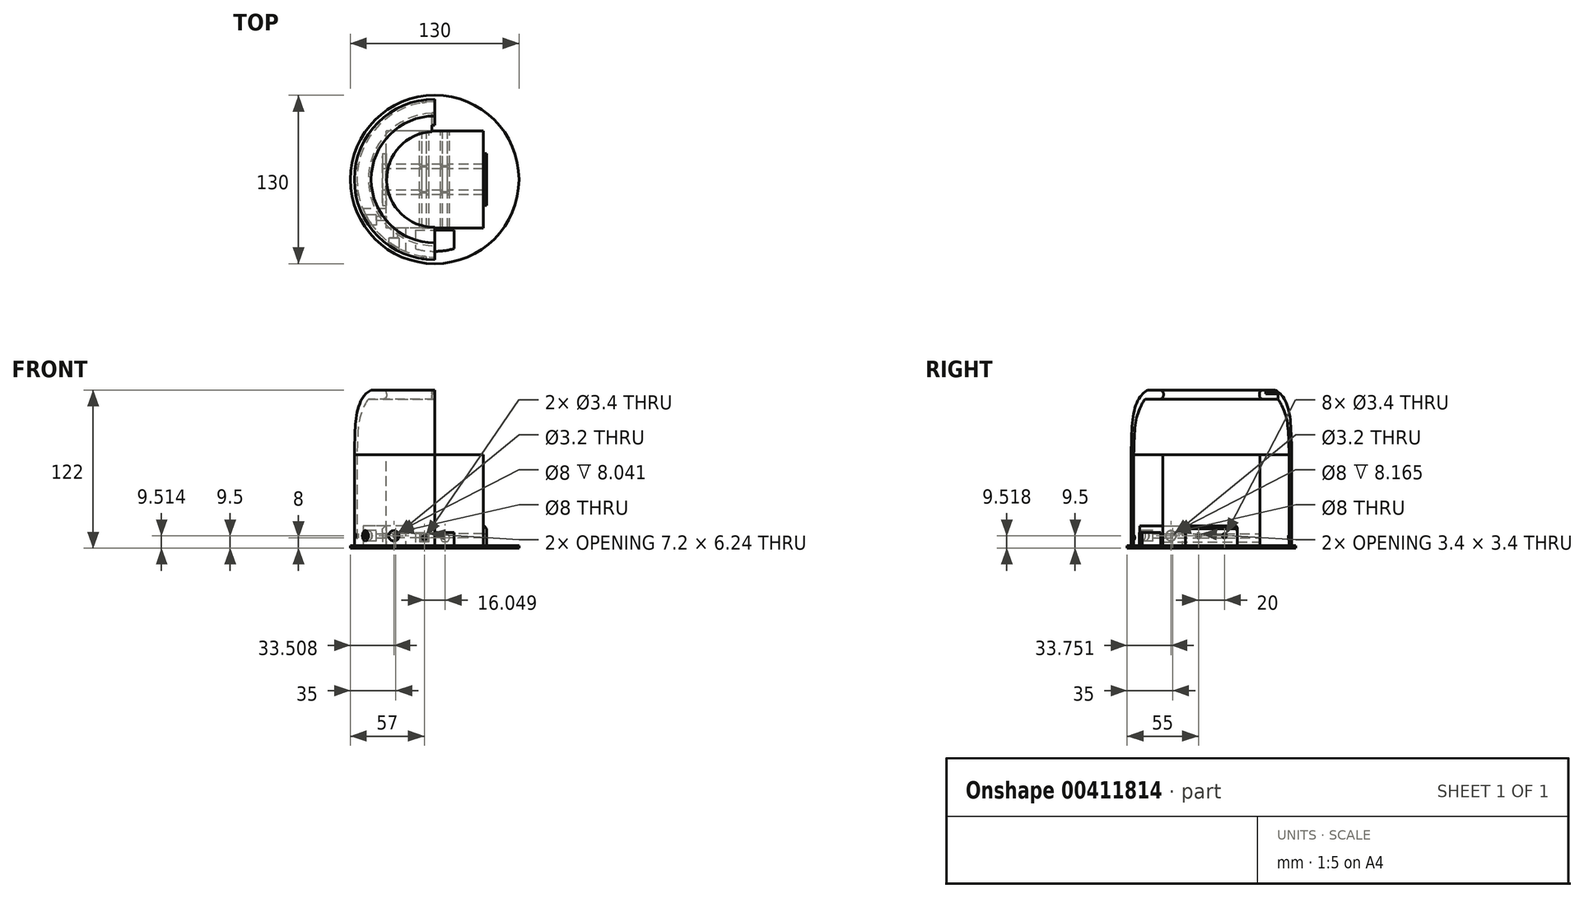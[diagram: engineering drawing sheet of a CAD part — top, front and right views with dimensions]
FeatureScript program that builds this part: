
annotation { "Feature Type Name" : "Feature", "Feature Type Description" : "" }
export const myFeature = defineFeature(function(context is Context, id is Id, definition is map)
    precondition{}
    {
        {
            var Q0;
            Q0=qCreatedBy(makeId("Front.planeOp"),FACE);
            var sketch = newSketch(context, id + "F0", { "sketchPlane" : qUnion([Q0])});
            skLineSegment(sketch, "E0", {"start": v(-40, 50) * mm, "end": v(-49, 50) * mm});
            skLineSegment(sketch, "E1", {"start": v(-62, 0) * mm, "end": v(-62, -70) * mm});
            skLineSegment(sketch, "E2", {"start": v(-37, 47) * mm, "end": v(-37, 46) * mm});
            skLineSegment(sketch, "E3", {"start": v(-40, 43) * mm, "end": v(-51.2, 43) * mm});
            skFitSpline(sketch, "E4", {"points": [v(-49, 50) * mm, v(-52.64, 47.47) * mm, v(-56.76, 41.98) * mm, v(-60.39, 29.9) * mm, v(-62, 0) * mm], "startDerivative": vector(-21.37, -10.6) * mm, "endDerivative": vector(-3.86, -109.3) * mm});
            skPoint(sketch, "E5.visualSharp", {"position": v(-37, 50) * mm});
            skArc(sketch, "E5.filletArc", {"start": v(-37, 47) * mm, "mid": v(-37.88, 49.12) * mm, "end": v(-40, 50) * mm});
            skPoint(sketch, "E6.visualSharp", {"position": v(-37, 43) * mm});
            skArc(sketch, "E6.filletArc", {"start": v(-40, 43) * mm, "mid": v(-37.88, 43.88) * mm, "end": v(-37, 46) * mm});
            skFitSpline(sketch, "E7", {"points": [v(-51.2, 43) * mm, v(-53.22, 40.09) * mm, v(-57.32, 30.2) * mm, v(-60, 0) * mm], "startDerivative": vector(-23.74, -33.12) * mm, "endDerivative": vector(-3.58, -89.87) * mm});
            skLineSegment(sketch, "E8", {"start": v(-62, -70) * mm, "end": v(0, -70) * mm});
            skLineSegment(sketch, "E9", {"start": v(0, -70) * mm, "end": v(0, -69.08) * mm});
            skLineSegment(sketch, "E10", {"start": v(-60, 0) * mm, "end": v(-60, -70) * mm});
            skSolve(sketch);
        }
        {
            var Q0;
            Q0=makeQuery(id+"F0.imprint","IMPRINT",FACE,{"disambiguationData":[TD([[makeQuery(id+"F0.imprint","IMPRINT",EDGE,{"derivedFrom":sQuery(id+"F0.wireOp",EDGE,"E0")}),1.0]])]});
            var Q1;
            Q1=sQuery(id+"F0.wireOp",EDGE,"E9");
            revolve(context, id + "F1", {"entities" : qUnion([Q0]), "axis" : qUnion([Q1]), "revolveType" : RevolveType.SYMMETRIC, "angle" : 180 * degree});
        }
        {
            var Q0;
            Q0=qCreatedBy(makeId("Front.planeOp"),FACE);
            var sketch = newSketch(context, id + "F2", { "sketchPlane" : qUnion([Q0])});
            skCircle(sketch, "E11", {"center": v(0, 47) * mm, "radius": 2 * mm});
            skLineSegment(sketch, "E12", {"start": v(-2, 47.07) * mm, "end": v(-2, 42.07) * mm});
            skLineSegment(sketch, "E13", {"start": v(-2, 42.07) * mm, "end": v(0, 42.07) * mm});
            skLineSegment(sketch, "E14", {"start": v(0, 42.07) * mm, "end": v(0, 45) * mm});
            skLineSegment(sketch, "E15", {"start": v(-2, 47.07) * mm, "end": v(-2, 50.36) * mm});
            skLineSegment(sketch, "E16", {"start": v(0, 50.36) * mm, "end": v(0, 49) * mm});
            skLineSegment(sketch, "E17", {"start": v(-2, 50.36) * mm, "end": v(0, 50.36) * mm});
            skSolve(sketch);
        }
        {
            var Q0;
            {var subQ1=sQuery(id+"F2.wireOp",EDGE,"E11");var subQ4=makeQuery(id+"F2.imprint","INTERSECT",VERTEX,{"derivedFrom":[subQ1,sQuery(id+"F2.wireOp",EDGE,"E14")]});Q0=makeQuery(id+"F2.imprint","IMPRINT",FACE,{"disambiguationData":[TD([[makeQuery(id+"F2.imprint","IMPRINT",EDGE,{"disambiguationData":[TD([[subQ4,1.0]])],"derivedFrom":subQ1}),1.0]])]});}
            extrude(context, id + "F3", {"entities" : qUnion([Q0]), "operationType" : NewBodyOperationType.REMOVE, "oppositeDirection" : true, "depth" : 49 * mm});
        }
        {
            var Q0;
            {var subQ0=sQuery(id+"F2.wireOp",EDGE,"E15");Q0=makeQuery(id+"F2.imprint","IMPRINT",FACE,{"disambiguationData":[TD([[makeQuery(id+"F2.imprint","IMPRINT",EDGE,{"derivedFrom":subQ0}),-1.0]])]});}
            extrude(context, id + "F4", {"entities" : qUnion([Q0]), "operationType" : NewBodyOperationType.REMOVE, "oppositeDirection" : true, "depth" : 42 * mm});
        }
        {
            var Q0;
            {var subQ4=sQuery(id+"F2.wireOp",EDGE,"E13");Q0=makeQuery(id+"F2.imprint","IMPRINT",FACE,{"disambiguationData":[TD([[makeQuery(id+"F2.imprint","IMPRINT",EDGE,{"derivedFrom":subQ4}),1.0]])]});}
            extrude(context, id + "F5", {"entities" : qUnion([Q0]), "operationType" : NewBodyOperationType.REMOVE, "oppositeDirection" : true, "depth" : 51.5 * mm});
        }
        {
            var Q0;
            Q0=qCreatedBy(makeId("Right.planeOp"),FACE);
            var sketch = newSketch(context, id + "F6", { "sketchPlane" : qUnion([Q0])});
            skLineSegment(sketch, "E18.bottom", {"start": v(49, 47) * mm, "end": v(51.5, 47) * mm});
            skLineSegment(sketch, "E18.top", {"start": v(49, 44) * mm, "end": v(51.5, 44) * mm});
            skLineSegment(sketch, "E18.left", {"start": v(49, 47) * mm, "end": v(49, 44) * mm});
            skLineSegment(sketch, "E18.right", {"start": v(51.5, 47) * mm, "end": v(51.5, 44) * mm});
            skSolve(sketch);
        }
        {
            var Q0;
            Q0=makeQuery(id+"F6.imprint","IMPRINT",FACE,{"disambiguationData":[TD([[makeQuery(id+"F6.imprint","IMPRINT",EDGE,{"derivedFrom":sQuery(id+"F6.wireOp",EDGE,"E18.bottom")}),-1.0]])]});
            extrude(context, id + "F7", {"entities" : qUnion([Q0]), "operationType" : NewBodyOperationType.REMOVE, "oppositeDirection" : true, "depth" : 2 * mm});
        }
        {
            var Q0;
            Q0=qCreatedBy(makeId("Top.planeOp"),FACE);
            var sketch = newSketch(context, id + "F8", { "sketchPlane" : qUnion([Q0])});
            skLineSegment(sketch, "E19.bottom", {"start": v(37.5, -37.5) * mm, "end": v(-37.5, -37.5) * mm});
            skLineSegment(sketch, "E19.top", {"start": v(37.5, 37.5) * mm, "end": v(-37.5, 37.5) * mm});
            skLineSegment(sketch, "E19.left", {"start": v(37.5, -37.5) * mm, "end": v(37.5, 37.5) * mm});
            skLineSegment(sketch, "E19.right", {"start": v(-37.5, -37.5) * mm, "end": v(-37.5, 37.5) * mm});
            skSolve(sketch);
        }
        {
            var Q0;
            Q0=makeQuery(id+"F8.imprint","IMPRINT",FACE,{"disambiguationData":[TD([[makeQuery(id+"F8.imprint","IMPRINT",EDGE,{"derivedFrom":sQuery(id+"F8.wireOp",EDGE,"E19.bottom")}),-1.0]])]});
            extrude(context, id + "F9", {"entities" : qUnion([Q0]), "operationType" : NewBodyOperationType.ADD, "oppositeDirection" : true, "depth" : 70 * mm});
        }
        {
            var Q0;
            Q0=makeQuery(id+"F9.opExtrude","CAP_FACE",FACE,{"disambiguationData":[OSD([sQuery(id+"F8.wireOp",EDGE,"E19.bottom"),sQuery(id+"F8.wireOp",EDGE,"E19.top"),sQuery(id+"F8.wireOp",EDGE,"E19.left"),sQuery(id+"F8.wireOp",EDGE,"E19.right")])],"isStart":false});
            var sketch = newSketch(context, id + "F10", { "sketchPlane" : qUnion([Q0])});
            skLineSegment(sketch, "E20", {"start": v(-37.5, 37.5) * mm, "end": v(-37.5, 22.5) * mm});
            skLineSegment(sketch, "E21", {"start": v(-37.5, 22.5) * mm, "end": v(-55.3, 22.5) * mm});
            skLineSegment(sketch, "E22", {"start": v(-37.5, 37.5) * mm, "end": v(-22.5, 37.5) * mm});
            skLineSegment(sketch, "E23", {"start": v(-22.5, 37.5) * mm, "end": v(-22.5, 55.3) * mm});
            skArc(sketch, "E24", {"start": v(-22.5, 55.3) * mm, "mid": v(-42.28, 42.28) * mm, "end": v(-55.3, 22.5) * mm});
            skSolve(sketch);
        }
        {
            var Q0;
            Q0=makeQuery(id+"F10.imprint","IMPRINT",FACE,{"disambiguationData":[TD([[makeQuery(id+"F10.imprint","IMPRINT",EDGE,{"derivedFrom":sQuery(id+"F10.wireOp",EDGE,"E20")}),-1.0]])]});
            extrude(context, id + "F11", {"entities" : qUnion([Q0]), "oppositeDirection" : true, "depth" : 15 * mm});
        }
        {
            var Q0;
            Q0=makeQuery(id+"F11.opExtrude","SWEPT_FACE",FACE,{"disambiguationData":[OSD([sQuery(id+"F10.wireOp",EDGE,"E20")])]});
            var sketch = newSketch(context, id + "F12", { "sketchPlane" : qUnion([Q0])});
            skCircle(sketch, "E25", {"center": v(-30, -62.5) * mm, "radius": 1.6 * mm});
            skSolve(sketch);
        }
        {
            var Q0;
            Q0=makeQuery(id+"F12.imprint","IMPRINT",FACE,{"disambiguationData":[TD([[makeQuery(id+"F12.imprint","IMPRINT",EDGE,{"derivedFrom":sQuery(id+"F12.wireOp",EDGE,"E25")}),1.0]])]});
            extrude(context, id + "F13", {"entities" : qUnion([Q0]), "operationType" : NewBodyOperationType.REMOVE, "oppositeDirection" : true, "depth" : 15 * mm});
        }
        {
            var Q0;
            Q0=qCreatedBy(makeId("Right.planeOp"),FACE);
            cPlane(context, id + "F14", {"entities" : qUnion([Q0]), "cplaneType" : CPlaneType.OFFSET, "offset" : 60 * mm, "oppositeDirection" : true, "width" : 150 * mm, "height" : 150 * mm});
        }
        {
            var Q0;
            Q0=qCreatedBy(id+"F14.planeOp",FACE);
            var sketch = newSketch(context, id + "F15", { "sketchPlane" : qUnion([Q0])});
            skCircle(sketch, "E26", {"center": v(-31.25, -62.48) * mm, "radius": 4 * mm});
            skSolve(sketch);
        }
        {
            var Q0;
            Q0=qSketchRegion(id+"F15",true);
            extrude(context, id + "F16", {"entities" : qUnion([Q0]), "operationType" : NewBodyOperationType.REMOVE, "depth" : 15 * mm});
        }
        {
            var Q0;
            Q0=makeQuery(id+"F11.opExtrude","SWEPT_FACE",FACE,{"disambiguationData":[OSD([sQuery(id+"F10.wireOp",EDGE,"E22")])]});
            var sketch = newSketch(context, id + "F17", { "sketchPlane" : qUnion([Q0])});
            skCircle(sketch, "E27", {"center": v(30, -62.5) * mm, "radius": 1.6 * mm});
            skSolve(sketch);
        }
        {
            var Q0;
            Q0=makeQuery(id+"F17.imprint","IMPRINT",FACE,{"disambiguationData":[TD([[makeQuery(id+"F17.imprint","IMPRINT",EDGE,{"derivedFrom":sQuery(id+"F17.wireOp",EDGE,"E27")}),1.0]])]});
            extrude(context, id + "F18", {"entities" : qUnion([Q0]), "operationType" : NewBodyOperationType.REMOVE, "oppositeDirection" : true, "depth" : 15 * mm});
        }
        {
            var Q0;
            Q0=qCreatedBy(makeId("Front.planeOp"),FACE);
            cPlane(context, id + "F19", {"entities" : qUnion([Q0]), "cplaneType" : CPlaneType.OFFSET, "offset" : 60 * mm, "width" : 150 * mm, "height" : 150 * mm});
        }
        {
            var Q0;
            Q0=qCreatedBy(id+"F19.planeOp",FACE);
            var sketch = newSketch(context, id + "F20", { "sketchPlane" : qUnion([Q0])});
            skCircle(sketch, "E28", {"center": v(-31.5, -62.49) * mm, "radius": 4 * mm});
            skSolve(sketch);
        }
        {
            var Q0;
            Q0=qSketchRegion(id+"F20",true);
            extrude(context, id + "F21", {"entities" : qUnion([Q0]), "operationType" : NewBodyOperationType.REMOVE, "oppositeDirection" : true, "depth" : 15 * mm});
        }
        {
            var Q0;
            Q0=qCreatedBy(makeId("Front.planeOp"),FACE);
            var sketch = newSketch(context, id + "F22", { "sketchPlane" : qUnion([Q0])});
            skLineSegment(sketch, "E29.bottom", {"start": v(0, -70) * mm, "end": v(-65, -70) * mm});
            skLineSegment(sketch, "E29.top", {"start": v(0, -72) * mm, "end": v(-65, -72) * mm});
            skLineSegment(sketch, "E29.left", {"start": v(0, -70) * mm, "end": v(0, -72) * mm});
            skLineSegment(sketch, "E29.right", {"start": v(-65, -70) * mm, "end": v(-65, -72) * mm});
            skLineSegment(sketch, "E30.bottom", {"start": v(-65, -70) * mm, "end": v(-62.25, -70) * mm});
            skLineSegment(sketch, "E30.top", {"start": v(-65, -67.15) * mm, "end": v(-62.25, -67.15) * mm});
            skLineSegment(sketch, "E30.left", {"start": v(-65, -70) * mm, "end": v(-65, -67.15) * mm});
            skLineSegment(sketch, "E30.right", {"start": v(-62.25, -70) * mm, "end": v(-62.25, -67.15) * mm});
            skLineSegment(sketch, "E31.bottom", {"start": v(-59.3, -70) * mm, "end": v(-55.5, -70) * mm});
            skLineSegment(sketch, "E31.top", {"start": v(-59.3, -60) * mm, "end": v(-55.5, -60) * mm});
            skLineSegment(sketch, "E31.left", {"start": v(-59.3, -70) * mm, "end": v(-59.3, -60) * mm});
            skLineSegment(sketch, "E31.right", {"start": v(-55.5, -70) * mm, "end": v(-55.5, -60) * mm});
            skSolve(sketch);
        }
        {
            var Q0;
            Q0=makeQuery(id+"F22.imprint","IMPRINT",FACE,{"disambiguationData":[TD([[makeQuery(id+"F22.imprint","IMPRINT",EDGE,{"derivedFrom":sQuery(id+"F22.wireOp",EDGE,"E30.bottom")}),1.0]])]});
            var Q1;
            Q1=makeQuery(id+"F22.imprint","IMPRINT",FACE,{"disambiguationData":[TD([[makeQuery(id+"F22.imprint","IMPRINT",EDGE,{"derivedFrom":sQuery(id+"F22.wireOp",EDGE,"E29.top")}),-1.0]])]});
            var Q2;
            Q2=makeQuery(id+"F22.imprint","IMPRINT",FACE,{"disambiguationData":[TD([[makeQuery(id+"F22.imprint","IMPRINT",EDGE,{"derivedFrom":sQuery(id+"F22.wireOp",EDGE,"E31.bottom")}),1.0]])]});
            var Q3;
            Q3=sQuery(id+"F0.wireOp",EDGE,"E9");
            revolve(context, id + "F23", {"entities" : qUnion([Q0, Q1, Q2]), "axis" : qUnion([Q3]), "revolveType" : RevolveType.FULL});
        }
        {
            var Q0;
            {var subQ0=sQuery(id+"F22.wireOp",EDGE,"E29.bottom");Q0=makeQuery(id+"F23.opRevolve","SWEPT_FACE",FACE,{"disambiguationData":[OSD([subQ0]),TDD([makeQuery(id+"F22.imprint","IMPRINT",EDGE,{"disambiguationData":[TD([[makeQuery(id+"F22.imprint","INTERSECT",VERTEX,{"derivedFrom":[subQ0,sQuery(id+"F22.wireOp",EDGE,"E29.left")]}),-1.0]])],"derivedFrom":subQ0})])]});}
            var sketch = newSketch(context, id + "F24", { "sketchPlane" : qUnion([Q0])});
            skLineSegment(sketch, "E32.bottom", {"start": v(-40.15, 20) * mm, "end": v(-37.55, 20) * mm});
            skLineSegment(sketch, "E32.top", {"start": v(-40.15, -20) * mm, "end": v(-37.55, -20) * mm});
            skLineSegment(sketch, "E32.left", {"start": v(-40.15, 20) * mm, "end": v(-40.15, -20) * mm});
            skLineSegment(sketch, "E32.right", {"start": v(-37.55, 20) * mm, "end": v(-37.55, -20) * mm});
            skSolve(sketch);
        }
        {
            var Q0;
            Q0=makeQuery(id+"F24.imprint","IMPRINT",FACE,{"disambiguationData":[TD([[makeQuery(id+"F24.imprint","IMPRINT",EDGE,{"derivedFrom":sQuery(id+"F24.wireOp",EDGE,"E32.bottom")}),-1.0]])]});
            extrude(context, id + "F25", {"entities" : qUnion([Q0]), "operationType" : NewBodyOperationType.ADD, "depth" : 15 * mm});
        }
        {
            var Q0;
            Q0=makeQuery(id+"F25.opExtrude","CAP_EDGE",EDGE,{"disambiguationData":[OSD([sQuery(id+"F24.wireOp",EDGE,"E32.left")])],"isStart":false});
            chamfer(context, id + "F26", {"entities" : qUnion([Q0]), "width" : 2 * mm, "tangentPropagation" : true});
        }
        {
            var Q0;
            Q0=makeQuery(id+"F26.opChamfer","BLEND_EDGE",EDGE,{"blendedFrom":[makeQuery(id+"F25.opExtrude","CAP_EDGE",EDGE,{"disambiguationData":[OSD([sQuery(id+"F24.wireOp",EDGE,"E32.left")])],"isStart":false}),makeQuery(id+"F25.opExtrude","SWEPT_FACE",FACE,{"disambiguationData":[OSD([sQuery(id+"F24.wireOp",EDGE,"E32.top")])]})],"blendedInto":[makeQuery(id+"F25.opExtrude","SWEPT_FACE",FACE,{"disambiguationData":[OSD([sQuery(id+"F24.wireOp",EDGE,"E32.top")])]})]});
            var Q1;
            Q1=makeQuery(id+"F26.opChamfer","BLEND_EDGE",EDGE,{"blendedFrom":[makeQuery(id+"F25.opExtrude","CAP_EDGE",EDGE,{"disambiguationData":[OSD([sQuery(id+"F24.wireOp",EDGE,"E32.left")])],"isStart":false}),makeQuery(id+"F25.opExtrude","SWEPT_FACE",FACE,{"disambiguationData":[OSD([sQuery(id+"F24.wireOp",EDGE,"E32.bottom")])]})],"blendedInto":[makeQuery(id+"F25.opExtrude","SWEPT_FACE",FACE,{"disambiguationData":[OSD([sQuery(id+"F24.wireOp",EDGE,"E32.bottom")])]})]});
            fillet(context, id + "F27", {"entities" : qUnion([Q0, Q1]), "radius" : 2 * mm, "tangentPropagation" : true, "allowEdgeOverflow" : false});
        }
        {
            var Q0;
            Q0=makeQuery(id+"F25.opExtrude","SWEPT_FACE",FACE,{"disambiguationData":[OSD([sQuery(id+"F24.wireOp",EDGE,"E32.left")])]});
            var sketch = newSketch(context, id + "F28", { "sketchPlane" : qUnion([Q0])});
            skCircle(sketch, "E33", {"center": v(-10, -62.5) * mm, "radius": 1.7 * mm});
            skCircle(sketch, "E34", {"center": v(10, -62.5) * mm, "radius": 1.7 * mm});
            skSolve(sketch);
        }
        {
            var Q0;
            Q0=makeQuery(id+"F28.imprint","IMPRINT",FACE,{"disambiguationData":[TD([[makeQuery(id+"F28.imprint","IMPRINT",EDGE,{"derivedFrom":sQuery(id+"F28.wireOp",EDGE,"E33")}),1.0]])]});
            var Q1;
            Q1=makeQuery(id+"F28.imprint","IMPRINT",FACE,{"disambiguationData":[TD([[makeQuery(id+"F28.imprint","IMPRINT",EDGE,{"derivedFrom":sQuery(id+"F28.wireOp",EDGE,"E34")}),1.0]])]});
            extrude(context, id + "F29", {"entities" : qUnion([Q0, Q1]), "operationType" : NewBodyOperationType.REMOVE, "endBound" : BoundingType.THROUGH_ALL, "oppositeDirection" : true, "depth" : 30 * mm});
        }
        {
            var Q0;
            {var subQ0=sQuery(id+"F22.wireOp",EDGE,"E29.bottom");Q0=makeQuery(id+"F23.opRevolve","SWEPT_FACE",FACE,{"disambiguationData":[OSD([subQ0]),TDD([makeQuery(id+"F22.imprint","IMPRINT",EDGE,{"disambiguationData":[TD([[makeQuery(id+"F22.imprint","INTERSECT",VERTEX,{"derivedFrom":[subQ0,sQuery(id+"F22.wireOp",EDGE,"E29.left")]}),-1.0]])],"derivedFrom":subQ0})])]});}
            var sketch = newSketch(context, id + "F30", { "sketchPlane" : qUnion([Q0])});
            skLineSegment(sketch, "E35.bottom", {"start": v(37.55, -20) * mm, "end": v(40.15, -20) * mm});
            skLineSegment(sketch, "E35.top", {"start": v(37.55, 20) * mm, "end": v(40.15, 20) * mm});
            skLineSegment(sketch, "E35.left", {"start": v(37.55, -20) * mm, "end": v(37.55, 20) * mm});
            skLineSegment(sketch, "E35.right", {"start": v(40.15, -20) * mm, "end": v(40.15, 20) * mm});
            skSolve(sketch);
        }
        {
            var Q0;
            Q0=makeQuery(id+"F30.imprint","IMPRINT",FACE,{"disambiguationData":[TD([[makeQuery(id+"F30.imprint","IMPRINT",EDGE,{"derivedFrom":sQuery(id+"F30.wireOp",EDGE,"E35.bottom")}),1.0]])]});
            extrude(context, id + "F31", {"entities" : qUnion([Q0]), "operationType" : NewBodyOperationType.ADD, "depth" : 15 * mm});
        }
        {
            var Q0;
            Q0=makeQuery(id+"F31.opExtrude","SWEPT_FACE",FACE,{"disambiguationData":[OSD([sQuery(id+"F30.wireOp",EDGE,"E35.right")])]});
            var sketch = newSketch(context, id + "F32", { "sketchPlane" : qUnion([Q0])});
            skCircle(sketch, "E36", {"center": v(-10, -62.5) * mm, "radius": 1.7 * mm});
            skCircle(sketch, "E37", {"center": v(10, -62.5) * mm, "radius": 1.7 * mm});
            skSolve(sketch);
        }
        {
            var Q0;
            Q0=makeQuery(id+"F32.imprint","IMPRINT",FACE,{"disambiguationData":[TD([[makeQuery(id+"F32.imprint","IMPRINT",EDGE,{"derivedFrom":sQuery(id+"F32.wireOp",EDGE,"E36")}),1.0]])]});
            var Q1;
            Q1=makeQuery(id+"F32.imprint","IMPRINT",FACE,{"disambiguationData":[TD([[makeQuery(id+"F32.imprint","IMPRINT",EDGE,{"derivedFrom":sQuery(id+"F32.wireOp",EDGE,"E37")}),1.0]])]});
            extrude(context, id + "F33", {"entities" : qUnion([Q0, Q1]), "operationType" : NewBodyOperationType.REMOVE, "endBound" : BoundingType.THROUGH_ALL, "oppositeDirection" : true, "depth" : 2.6 * mm});
        }
        {
            var Q0;
            Q0=makeQuery(id+"F31.opExtrude","CAP_EDGE",EDGE,{"disambiguationData":[OSD([sQuery(id+"F30.wireOp",EDGE,"E35.right")])],"isStart":false});
            chamfer(context, id + "F34", {"entities" : qUnion([Q0]), "width" : 2 * mm, "tangentPropagation" : true});
        }
        {
            var Q0;
            Q0=makeQuery(id+"F34.opChamfer","BLEND_EDGE",EDGE,{"blendedFrom":[makeQuery(id+"F31.opExtrude","CAP_EDGE",EDGE,{"disambiguationData":[OSD([sQuery(id+"F30.wireOp",EDGE,"E35.right")])],"isStart":false}),makeQuery(id+"F31.opExtrude","SWEPT_FACE",FACE,{"disambiguationData":[OSD([sQuery(id+"F30.wireOp",EDGE,"E35.bottom")])]})],"blendedInto":[makeQuery(id+"F31.opExtrude","SWEPT_FACE",FACE,{"disambiguationData":[OSD([sQuery(id+"F30.wireOp",EDGE,"E35.bottom")])]})]});
            var Q1;
            Q1=makeQuery(id+"F34.opChamfer","BLEND_EDGE",EDGE,{"blendedFrom":[makeQuery(id+"F31.opExtrude","CAP_EDGE",EDGE,{"disambiguationData":[OSD([sQuery(id+"F30.wireOp",EDGE,"E35.right")])],"isStart":false}),makeQuery(id+"F31.opExtrude","SWEPT_FACE",FACE,{"disambiguationData":[OSD([sQuery(id+"F30.wireOp",EDGE,"E35.top")])]})],"blendedInto":[makeQuery(id+"F31.opExtrude","SWEPT_FACE",FACE,{"disambiguationData":[OSD([sQuery(id+"F30.wireOp",EDGE,"E35.top")])]})]});
            fillet(context, id + "F35", {"entities" : qUnion([Q0, Q1]), "radius" : 2 * mm, "tangentPropagation" : true, "allowEdgeOverflow" : false});
        }
        {
            var Q0;
            Q0=qCreatedBy(makeId("Front.planeOp"),FACE);
            var sketch = newSketch(context, id + "F36", { "sketchPlane" : qUnion([Q0])});
            skCircle(sketch, "E38", {"center": v(-8, -64) * mm, "radius": 1.7 * mm});
            skCircle(sketch, "E39", {"center": v(8, -64) * mm, "radius": 1.7 * mm});
            skSolve(sketch);
        }
        {
            var Q0;
            Q0=makeQuery(id+"F36.imprint","IMPRINT",FACE,{"disambiguationData":[TD([[makeQuery(id+"F36.imprint","IMPRINT",EDGE,{"derivedFrom":sQuery(id+"F36.wireOp",EDGE,"E38")}),1.0]])]});
            var Q1;
            Q1=makeQuery(id+"F36.imprint","IMPRINT",FACE,{"disambiguationData":[TD([[makeQuery(id+"F36.imprint","IMPRINT",EDGE,{"derivedFrom":sQuery(id+"F36.wireOp",EDGE,"E39")}),1.0]])]});
            extrude(context, id + "F37", {"entities" : qUnion([Q0, Q1]), "operationType" : NewBodyOperationType.REMOVE, "depth" : 130 * mm, "symmetric" : true});
        }
        {
            var Q0;
            Q0=makeQuery(id+"F36.imprint","IMPRINT",FACE,{"disambiguationData":[TD([[makeQuery(id+"F36.imprint","IMPRINT",EDGE,{"derivedFrom":sQuery(id+"F36.wireOp",EDGE,"E39")}),1.0]])]});
            var sketch = newSketch(context, id + "F38", { "sketchPlane" : qUnion([Q0])});
            skCircle(sketch, "E40", {"center": v(8.05, -64) * mm, "radius": 3.6 * mm});
            skCircle(sketch, "E41", {"center": v(-8, -64) * mm, "radius": 3.6 * mm});
            skCircle(sketch, "E42.cCircle", {"center": v(8.05, -64) * mm, "radius": 3.6 * mm, "construction": true});
            skLineSegment(sketch, "E42.0", {"start": v(9.85, -60.88) * mm, "end": v(11.65, -64) * mm});
            skLineSegment(sketch, "E42.1", {"start": v(11.65, -64) * mm, "end": v(9.85, -67.11) * mm});
            skLineSegment(sketch, "E42.2", {"start": v(9.85, -67.11) * mm, "end": v(6.25, -67.11) * mm});
            skLineSegment(sketch, "E42.3", {"start": v(6.25, -67.11) * mm, "end": v(4.45, -64) * mm});
            skLineSegment(sketch, "E42.4", {"start": v(4.45, -64) * mm, "end": v(6.25, -60.88) * mm});
            skLineSegment(sketch, "E42.5", {"start": v(6.25, -60.88) * mm, "end": v(9.85, -60.88) * mm});
            skCircle(sketch, "E43.cCircle", {"center": v(-8, -64) * mm, "radius": 3.6 * mm, "construction": true});
            skLineSegment(sketch, "E43.0", {"start": v(-6.2, -60.88) * mm, "end": v(-4.4, -64) * mm});
            skLineSegment(sketch, "E43.1", {"start": v(-4.4, -64) * mm, "end": v(-6.2, -67.12) * mm});
            skLineSegment(sketch, "E43.2", {"start": v(-6.2, -67.12) * mm, "end": v(-9.8, -67.12) * mm});
            skLineSegment(sketch, "E43.3", {"start": v(-9.8, -67.12) * mm, "end": v(-11.6, -64) * mm});
            skLineSegment(sketch, "E43.4", {"start": v(-11.6, -64) * mm, "end": v(-9.8, -60.88) * mm});
            skLineSegment(sketch, "E43.5", {"start": v(-9.8, -60.88) * mm, "end": v(-6.2, -60.88) * mm});
            skSolve(sketch);
        }
        {
            var Q0;
            Q0=makeQuery(id+"F38.imprint","IMPRINT",FACE,{"disambiguationData":[TD([[makeQuery(id+"F38.imprint","IMPRINT",EDGE,{"derivedFrom":makeQuery(id+"F36.imprint","IMPRINT",EDGE,{"derivedFrom":sQuery(id+"F36.wireOp",EDGE,"E39")})}),-1.0]])]});
            var Q1;
            Q1=makeQuery(id+"F38.imprint","IMPRINT",FACE,{"disambiguationData":[TD([[makeQuery(id+"F38.imprint","IMPRINT",EDGE,{"derivedFrom":sQuery(id+"F38.wireOp",EDGE,"E43.0")}),-1.0]])]});
            var Q2;
            Q2=sQuery(id+"F38.wireOp",EDGE,"E40");
            var Q3;
            Q3=sQuery(id+"F38.wireOp",EDGE,"E41");
            extrude(context, id + "F39", {"entities" : qUnion([Q0, Q1]), "operationType" : NewBodyOperationType.REMOVE, "surfaceEntities" : qUnion([Q2, Q3]), "depth" : 115 * mm, "symmetric" : true});
        }
        {
            var Q0;
            Q0=makeQuery(id+"F24.imprint","IMPRINT",FACE,{"disambiguationData":[TD([[makeQuery(id+"F24.imprint","IMPRINT",EDGE,{"derivedFrom":sQuery(id+"F24.wireOp",EDGE,"E32.bottom")}),1.0]])]});
            var sketch = newSketch(context, id + "F40", { "sketchPlane" : qUnion([Q0])});
            skLineSegment(sketch, "E44", {"start": v(-15, -38.93) * mm, "end": v(15, -38.93) * mm});
            skLineSegment(sketch, "E45", {"start": v(15, -38.93) * mm, "end": v(15, -53.43) * mm});
            skLineSegment(sketch, "E46", {"start": v(-15, -38.93) * mm, "end": v(-15, -53.43) * mm});
            skArc(sketch, "E47", {"start": v(-15, -53.43) * mm, "mid": v(0, -55.5) * mm, "end": v(15, -53.43) * mm});
            skSolve(sketch);
        }
        {
            var Q0;
            Q0=makeQuery(id+"F40.imprint","IMPRINT",FACE,{"disambiguationData":[TD([[makeQuery(id+"F40.imprint","IMPRINT",EDGE,{"derivedFrom":sQuery(id+"F40.wireOp",EDGE,"E44")}),-1.0]])]});
            var Q1;
            Q1=sQuery(id+"F40.wireOp",EDGE,"E45");
            var Q2;
            Q2=sQuery(id+"F40.wireOp",EDGE,"E47");
            var Q3;
            Q3=sQuery(id+"F40.wireOp",EDGE,"E46");
            var Q4;
            Q4=sQuery(id+"F40.wireOp",EDGE,"E44");
            extrude(context, id + "F41", {"entities" : qUnion([Q0]), "surfaceEntities" : qUnion([Q1, Q2, Q3, Q4]), "depth" : 10 * mm});
        }
    });
